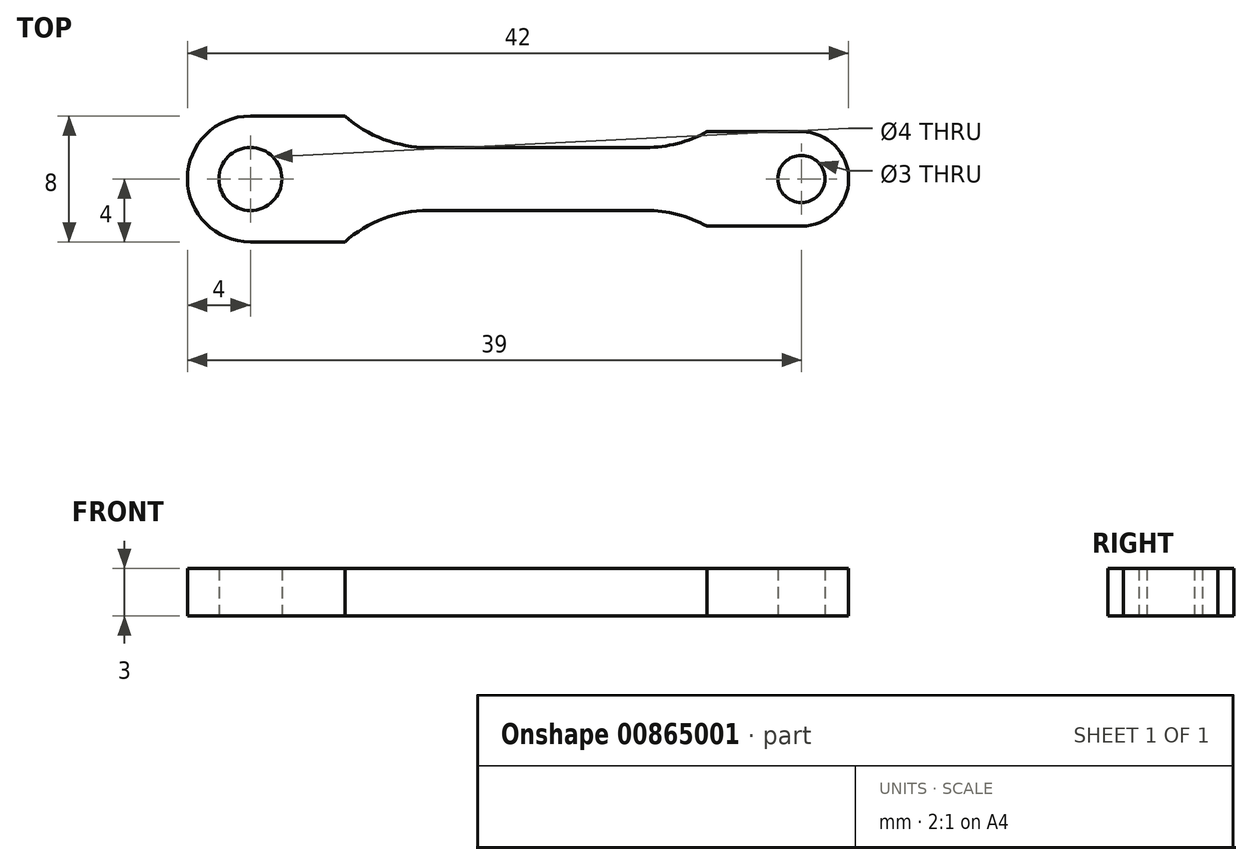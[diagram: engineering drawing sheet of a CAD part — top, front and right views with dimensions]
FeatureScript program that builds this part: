
annotation { "Feature Type Name" : "Feature", "Feature Type Description" : "" }
export const myFeature = defineFeature(function(context is Context, id is Id, definition is map)
    precondition{}
    {
        {
            var Q0;
            Q0=qCreatedBy(makeId("Top.planeOp"),FACE);
            var sketch = newSketch(context, id + "F0", { "sketchPlane" : qUnion([Q0])});
            skArc(sketch, "E0", {"start": v(0, 4) * mm, "mid": v(-4, 0) * mm, "end": v(0, -4) * mm});
            skCircle(sketch, "E1", {"center": v(0, 0) * mm, "radius": 2 * mm});
            skCircle(sketch, "E2", {"center": v(35, 0) * mm, "radius": 1.5 * mm});
            skArc(sketch, "E3", {"start": v(35, -3) * mm, "mid": v(38, 0) * mm, "end": v(35, 3) * mm});
            skLineSegment(sketch, "E4", {"start": v(0, 4) * mm, "end": v(6, 4) * mm});
            skLineSegment(sketch, "E5", {"start": v(35, 3) * mm, "end": v(29, 3) * mm});
            skLineSegment(sketch, "E6", {"start": v(11.3, 2) * mm, "end": v(25.13, 2) * mm});
            skArc(sketch, "E7", {"start": v(6, 4) * mm, "mid": v(8.46, 2.52) * mm, "end": v(11.3, 2) * mm});
            skArc(sketch, "E8", {"start": v(25.13, 2) * mm, "mid": v(27.13, 2.25) * mm, "end": v(29, 3) * mm});
            skLineSegment(sketch, "E9.MirrorCS", {"start": v(0, -4) * mm, "end": v(6, -4) * mm});
            skArc(sketch, "E10.MirrorCS", {"start": v(6, -4) * mm, "mid": v(8.46, -2.52) * mm, "end": v(11.3, -2) * mm});
            skLineSegment(sketch, "E11.MirrorCS", {"start": v(11.3, -2) * mm, "end": v(25.13, -2) * mm});
            skArc(sketch, "E12.MirrorCS", {"start": v(25.13, -2) * mm, "mid": v(27.13, -2.25) * mm, "end": v(29, -3) * mm});
            skLineSegment(sketch, "E13.MirrorCS", {"start": v(35, -3) * mm, "end": v(29, -3) * mm});
            skSolve(sketch);
        }
        {
            var Q0;
            Q0=makeQuery(id+"F0.imprint","IMPRINT",FACE,{"disambiguationData":[TD([[makeQuery(id+"F0.imprint","IMPRINT",EDGE,{"derivedFrom":sQuery(id+"F0.wireOp",EDGE,"E0")}),1.0]])]});
            extrude(context, id + "F1", {"entities" : qUnion([Q0]), "depth" : 3 * mm, "offsetDistance" : 25 * mm});
        }
    });
